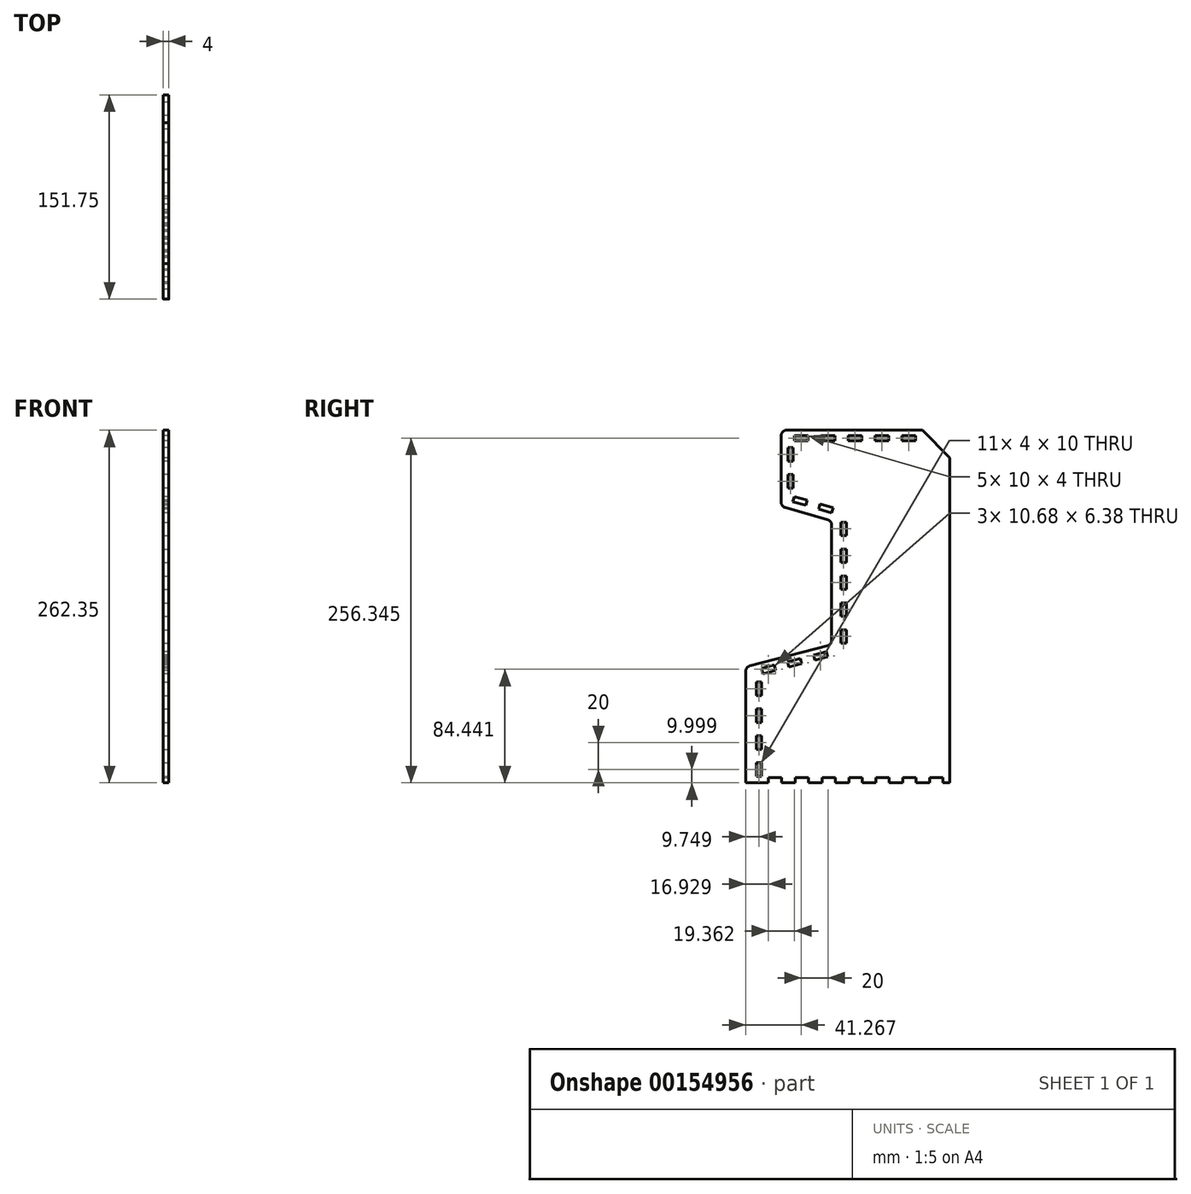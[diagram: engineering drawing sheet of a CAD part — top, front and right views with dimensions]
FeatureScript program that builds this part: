
annotation { "Feature Type Name" : "Feature", "Feature Type Description" : "" }
export const myFeature = defineFeature(function(context is Context, id is Id, definition is map)
    precondition{}
    {
        {
            var Q0;
            Q0=qCreatedBy(makeId("Right.planeOp"),FACE);
            var sketch = newSketch(context, id + "F0", { "sketchPlane" : qUnion([Q0])});
            skLineSegment(sketch, "E0", {"start": v(0, 0) * mm, "end": v(-63.83, -16.52) * mm});
            skLineSegment(sketch, "E1", {"start": v(-63.83, -16.52) * mm, "end": v(-63.83, -102.78) * mm});
            skLineSegment(sketch, "E2", {"start": v(-63.83, -102.78) * mm, "end": v(87.92, -102.78) * mm});
            skLineSegment(sketch, "E3", {"start": v(0, 0) * mm, "end": v(1, -3.87) * mm});
            skLineSegment(sketch, "E4", {"start": v(1, -3.87) * mm, "end": v(-3.84, -5.13) * mm});
            skLineSegment(sketch, "E5", {"start": v(-3.84, -5.13) * mm, "end": v(-13.52, -7.63) * mm});
            skLineSegment(sketch, "E6", {"start": v(-13.52, -7.63) * mm, "end": v(-23.2, -10.14) * mm});
            skLineSegment(sketch, "E7", {"start": v(-23.2, -10.14) * mm, "end": v(-32.88, -12.64) * mm});
            skLineSegment(sketch, "E8", {"start": v(-32.88, -12.64) * mm, "end": v(-42.56, -15.15) * mm});
            skLineSegment(sketch, "E9", {"start": v(-42.56, -15.15) * mm, "end": v(-52.24, -17.66) * mm});
            skLineSegment(sketch, "E10", {"start": v(-52.24, -17.66) * mm, "end": v(-61.92, -20.16) * mm});
            skLineSegment(sketch, "E11", {"start": v(-13.52, -7.63) * mm, "end": v(-12.52, -11.5) * mm});
            skLineSegment(sketch, "E12", {"start": v(-12.52, -11.5) * mm, "end": v(-2.84, -9) * mm});
            skLineSegment(sketch, "E13", {"start": v(-2.84, -9) * mm, "end": v(-3.84, -5.13) * mm});
            skLineSegment(sketch, "E14", {"start": v(-32.88, -12.64) * mm, "end": v(-31.88, -16.52) * mm});
            skLineSegment(sketch, "E15", {"start": v(-31.88, -16.52) * mm, "end": v(-22.2, -14) * mm});
            skLineSegment(sketch, "E16", {"start": v(-22.2, -14) * mm, "end": v(-23.2, -10.14) * mm});
            skLineSegment(sketch, "E17", {"start": v(-52.24, -17.66) * mm, "end": v(-51.24, -21.53) * mm});
            skLineSegment(sketch, "E18", {"start": v(-51.24, -21.53) * mm, "end": v(-41.56, -19.02) * mm});
            skLineSegment(sketch, "E19", {"start": v(-41.56, -19.02) * mm, "end": v(-42.56, -15.15) * mm});
            skLineSegment(sketch, "E20", {"start": v(0, 0) * mm, "end": v(0, 92.13) * mm});
            skLineSegment(sketch, "E21", {"start": v(87.92, -102.78) * mm, "end": v(87.92, 92.13) * mm});
            skLineSegment(sketch, "E22", {"start": v(0, 92.13) * mm, "end": v(87.92, 92.13) * mm});
            skSolve(sketch);
        }
        {
            var Q0;
            Q0 = qSketchRegion(id + "F0", true);
            extrude(context, id + "F1", {"entities" : qUnion([Q0]), "depth" : 4 * mm});
        }
        {
            var Q0;
            Q0=makeQuery(id+"F1.opExtrude","SWEPT_EDGE",EDGE,{"disambiguationData":[OSD([sQuery(id+"F0.wireOp",EDGE,"E0"),sQuery(id+"F0.wireOp",EDGE,"E1")])]});
            fillet(context, id + "F2", {"entities" : qUnion([Q0]), "radius" : 4 * mm, "tangentPropagation" : true, "allowEdgeOverflow" : false});
        }
        {
            var Q0;
            Q0=makeQuery(id+"F1.opExtrude","CAP_FACE",FACE,{"disambiguationData":[OSD([sQuery(id+"F0.wireOp",EDGE,"E0"),sQuery(id+"F0.wireOp",EDGE,"E1"),sQuery(id+"F0.wireOp",EDGE,"E2"),sQuery(id+"F0.wireOp",EDGE,"E5"),sQuery(id+"F0.wireOp",EDGE,"E7"),sQuery(id+"F0.wireOp",EDGE,"E9"),sQuery(id+"F0.wireOp",EDGE,"E11"),sQuery(id+"F0.wireOp",EDGE,"E12"),sQuery(id+"F0.wireOp",EDGE,"E13"),sQuery(id+"F0.wireOp",EDGE,"E14"),sQuery(id+"F0.wireOp",EDGE,"E15"),sQuery(id+"F0.wireOp",EDGE,"E16"),sQuery(id+"F0.wireOp",EDGE,"E17"),sQuery(id+"F0.wireOp",EDGE,"E18"),sQuery(id+"F0.wireOp",EDGE,"E19"),sQuery(id+"F0.wireOp",EDGE,"E20"),sQuery(id+"F0.wireOp",EDGE,"E21"),sQuery(id+"F0.wireOp",EDGE,"E22")])],"isStart":false});
            var sketch = newSketch(context, id + "F3", { "sketchPlane" : qUnion([Q0])});
            skLineSegment(sketch, "E23", {"start": v(-3.84, -5.13) * mm, "end": v(1, -3.87) * mm});
            skLineSegment(sketch, "E24", {"start": v(1, -3.87) * mm, "end": v(7, -3.87) * mm});
            skLineSegment(sketch, "E25", {"start": v(7, -3.87) * mm, "end": v(7, 92.13) * mm});
            skLineSegment(sketch, "E26", {"start": v(7, -3.87) * mm, "end": v(7, 1.13) * mm});
            skLineSegment(sketch, "E27", {"start": v(7, 1.13) * mm, "end": v(11, 1.13) * mm});
            skLineSegment(sketch, "E28", {"start": v(11, 1.13) * mm, "end": v(11, 11.13) * mm});
            skLineSegment(sketch, "E29", {"start": v(11, 11.13) * mm, "end": v(7, 11.13) * mm});
            skLineSegment(sketch, "E30.0.1.0", {"start": v(11, 31.13) * mm, "end": v(7, 31.13) * mm});
            skLineSegment(sketch, "E30.0.1.1", {"start": v(11, 21.13) * mm, "end": v(11, 31.13) * mm});
            skLineSegment(sketch, "E30.0.1.2", {"start": v(7, 21.13) * mm, "end": v(11, 21.13) * mm});
            skLineSegment(sketch, "E30.0.2.0", {"start": v(11, 51.13) * mm, "end": v(7, 51.13) * mm});
            skLineSegment(sketch, "E30.0.2.1", {"start": v(11, 41.13) * mm, "end": v(11, 51.13) * mm});
            skLineSegment(sketch, "E30.0.2.2", {"start": v(7, 41.13) * mm, "end": v(11, 41.13) * mm});
            skLineSegment(sketch, "E30.0.3.0", {"start": v(11, 71.13) * mm, "end": v(7, 71.13) * mm});
            skLineSegment(sketch, "E30.0.3.1", {"start": v(11, 61.13) * mm, "end": v(11, 71.13) * mm});
            skLineSegment(sketch, "E30.0.3.2", {"start": v(7, 61.13) * mm, "end": v(11, 61.13) * mm});
            skLineSegment(sketch, "E30.direction1", {"start": v(7, 11.13) * mm, "end": v(30, 11.13) * mm, "construction": true});
            skLineSegment(sketch, "E30.direction2", {"start": v(7, 11.13) * mm, "end": v(7, 31.13) * mm, "construction": true});
            skLineSegment(sketch, "E31.0.0.4", {"start": v(11, 91.13) * mm, "end": v(7, 91.13) * mm});
            skLineSegment(sketch, "E31.3.0.4", {"start": v(11, 81.13) * mm, "end": v(11, 91.13) * mm});
            skLineSegment(sketch, "E31.6.0.4", {"start": v(7, 81.13) * mm, "end": v(11, 81.13) * mm});
            skLineSegment(sketch, "E32", {"start": v(7, 91.13) * mm, "end": v(7, 81.13) * mm});
            skSolve(sketch);
        }
        {
            var Q0;
            Q0 = qSketchRegion(id + "F3", true);
            extrude(context, id + "F4", {"entities" : qUnion([Q0]), "operationType" : NewBodyOperationType.REMOVE, "oppositeDirection" : true, "depth" : 4 * mm});
        }
        {
            var Q0;
            Q0=makeQuery(id+"F1.opExtrude","CAP_FACE",FACE,{"disambiguationData":[OSD([sQuery(id+"F0.wireOp",EDGE,"E0"),sQuery(id+"F0.wireOp",EDGE,"E1"),sQuery(id+"F0.wireOp",EDGE,"E2"),sQuery(id+"F0.wireOp",EDGE,"E5"),sQuery(id+"F0.wireOp",EDGE,"E7"),sQuery(id+"F0.wireOp",EDGE,"E9"),sQuery(id+"F0.wireOp",EDGE,"E11"),sQuery(id+"F0.wireOp",EDGE,"E12"),sQuery(id+"F0.wireOp",EDGE,"E13"),sQuery(id+"F0.wireOp",EDGE,"E14"),sQuery(id+"F0.wireOp",EDGE,"E15"),sQuery(id+"F0.wireOp",EDGE,"E16"),sQuery(id+"F0.wireOp",EDGE,"E17"),sQuery(id+"F0.wireOp",EDGE,"E18"),sQuery(id+"F0.wireOp",EDGE,"E19"),sQuery(id+"F0.wireOp",EDGE,"E20"),sQuery(id+"F0.wireOp",EDGE,"E21"),sQuery(id+"F0.wireOp",EDGE,"E22")])],"isStart":false});
            var sketch = newSketch(context, id + "F5", { "sketchPlane" : qUnion([Q0])});
            skLineSegment(sketch, "E33", {"start": v(-51.24, -21.53) * mm, "end": v(-56.08, -22.78) * mm});
            skLineSegment(sketch, "E34", {"start": v(-56.08, -22.78) * mm, "end": v(-56.08, -27.78) * mm});
            skLineSegment(sketch, "E35", {"start": v(-56.08, -27.78) * mm, "end": v(-52.08, -27.78) * mm});
            skLineSegment(sketch, "E36", {"start": v(-56.08, -27.78) * mm, "end": v(-56.08, -37.78) * mm});
            skLineSegment(sketch, "E37", {"start": v(-56.08, -37.78) * mm, "end": v(-52.08, -37.78) * mm});
            skLineSegment(sketch, "E38", {"start": v(-52.08, -27.78) * mm, "end": v(-52.08, -37.78) * mm});
            skLineSegment(sketch, "E39.0.1.0", {"start": v(-52.08, -47.78) * mm, "end": v(-52.08, -57.78) * mm});
            skLineSegment(sketch, "E39.0.1.1", {"start": v(-56.08, -47.78) * mm, "end": v(-52.08, -47.78) * mm});
            skLineSegment(sketch, "E39.0.1.2", {"start": v(-56.08, -47.78) * mm, "end": v(-56.08, -57.78) * mm});
            skLineSegment(sketch, "E39.0.1.3", {"start": v(-56.08, -57.78) * mm, "end": v(-52.08, -57.78) * mm});
            skLineSegment(sketch, "E39.0.2.0", {"start": v(-52.08, -67.78) * mm, "end": v(-52.08, -77.78) * mm});
            skLineSegment(sketch, "E39.0.2.1", {"start": v(-56.08, -67.78) * mm, "end": v(-52.08, -67.78) * mm});
            skLineSegment(sketch, "E39.0.2.2", {"start": v(-56.08, -67.78) * mm, "end": v(-56.08, -77.78) * mm});
            skLineSegment(sketch, "E39.0.2.3", {"start": v(-56.08, -77.78) * mm, "end": v(-52.08, -77.78) * mm});
            skLineSegment(sketch, "E39.0.3.0", {"start": v(-52.08, -87.78) * mm, "end": v(-52.08, -97.78) * mm});
            skLineSegment(sketch, "E39.0.3.1", {"start": v(-56.08, -87.78) * mm, "end": v(-52.08, -87.78) * mm});
            skLineSegment(sketch, "E39.0.3.2", {"start": v(-56.08, -87.78) * mm, "end": v(-56.08, -97.78) * mm});
            skLineSegment(sketch, "E39.0.3.3", {"start": v(-56.08, -97.78) * mm, "end": v(-52.08, -97.78) * mm});
            skLineSegment(sketch, "E39.direction1", {"start": v(-52.08, -37.78) * mm, "end": v(-27.08, -37.78) * mm, "construction": true});
            skLineSegment(sketch, "E39.direction2", {"start": v(-52.08, -37.78) * mm, "end": v(-52.08, -57.78) * mm, "construction": true});
            skLineSegment(sketch, "E40", {"start": v(-52.08, -97.78) * mm, "end": v(-52.08, -102.78) * mm});
            skLineSegment(sketch, "E41", {"start": v(-52.08, -102.78) * mm, "end": v(-47.08, -102.78) * mm});
            skLineSegment(sketch, "E42.bottom", {"start": v(-47.08, -102.78) * mm, "end": v(-37.08, -102.78) * mm});
            skLineSegment(sketch, "E42.top", {"start": v(-47.08, -98.78) * mm, "end": v(-37.08, -98.78) * mm});
            skLineSegment(sketch, "E42.left", {"start": v(-47.08, -102.78) * mm, "end": v(-47.08, -98.78) * mm});
            skLineSegment(sketch, "E42.right", {"start": v(-37.08, -102.78) * mm, "end": v(-37.08, -98.78) * mm});
            skLineSegment(sketch, "E43.1.0.0", {"start": v(-27.08, -102.78) * mm, "end": v(-17.08, -102.78) * mm});
            skLineSegment(sketch, "E43.1.0.1", {"start": v(-17.08, -102.78) * mm, "end": v(-17.08, -98.78) * mm});
            skLineSegment(sketch, "E43.1.0.2", {"start": v(-27.08, -98.78) * mm, "end": v(-17.08, -98.78) * mm});
            skLineSegment(sketch, "E43.1.0.3", {"start": v(-27.08, -102.78) * mm, "end": v(-27.08, -98.78) * mm});
            skLineSegment(sketch, "E43.2.0.0", {"start": v(-7.08, -102.78) * mm, "end": v(2.92, -102.78) * mm});
            skLineSegment(sketch, "E43.2.0.1", {"start": v(2.92, -102.78) * mm, "end": v(2.92, -98.78) * mm});
            skLineSegment(sketch, "E43.2.0.2", {"start": v(-7.08, -98.78) * mm, "end": v(2.92, -98.78) * mm});
            skLineSegment(sketch, "E43.2.0.3", {"start": v(-7.08, -102.78) * mm, "end": v(-7.08, -98.78) * mm});
            skLineSegment(sketch, "E43.3.0.0", {"start": v(12.92, -102.78) * mm, "end": v(22.92, -102.78) * mm});
            skLineSegment(sketch, "E43.3.0.1", {"start": v(22.92, -102.78) * mm, "end": v(22.92, -98.78) * mm});
            skLineSegment(sketch, "E43.3.0.2", {"start": v(12.92, -98.78) * mm, "end": v(22.92, -98.78) * mm});
            skLineSegment(sketch, "E43.3.0.3", {"start": v(12.92, -102.78) * mm, "end": v(12.92, -98.78) * mm});
            skLineSegment(sketch, "E43.4.0.0", {"start": v(32.92, -102.78) * mm, "end": v(42.92, -102.78) * mm});
            skLineSegment(sketch, "E43.4.0.1", {"start": v(42.92, -102.78) * mm, "end": v(42.92, -98.78) * mm});
            skLineSegment(sketch, "E43.4.0.2", {"start": v(32.92, -98.78) * mm, "end": v(42.92, -98.78) * mm});
            skLineSegment(sketch, "E43.4.0.3", {"start": v(32.92, -102.78) * mm, "end": v(32.92, -98.78) * mm});
            skLineSegment(sketch, "E43.direction1", {"start": v(-47.08, -102.78) * mm, "end": v(-27.08, -102.78) * mm, "construction": true});
            skLineSegment(sketch, "E44.0.5.0", {"start": v(52.92, -102.78) * mm, "end": v(62.92, -102.78) * mm});
            skLineSegment(sketch, "E44.3.5.0", {"start": v(62.92, -102.78) * mm, "end": v(62.92, -98.78) * mm});
            skLineSegment(sketch, "E44.6.5.0", {"start": v(52.92, -98.78) * mm, "end": v(62.92, -98.78) * mm});
            skLineSegment(sketch, "E44.9.5.0", {"start": v(52.92, -102.78) * mm, "end": v(52.92, -98.78) * mm});
            skLineSegment(sketch, "E44.0.6.0", {"start": v(72.92, -102.78) * mm, "end": v(82.92, -102.78) * mm});
            skLineSegment(sketch, "E44.3.6.0", {"start": v(82.92, -102.78) * mm, "end": v(82.92, -98.78) * mm});
            skLineSegment(sketch, "E44.6.6.0", {"start": v(72.92, -98.78) * mm, "end": v(82.92, -98.78) * mm});
            skLineSegment(sketch, "E44.9.6.0", {"start": v(72.92, -102.78) * mm, "end": v(72.92, -98.78) * mm});
            skSolve(sketch);
        }
        {
            var Q0;
            Q0=makeQuery(id+"F5.imprint","IMPRINT",FACE,{"disambiguationData":[TD([[makeQuery(id+"F5.imprint","IMPRINT",EDGE,{"derivedFrom":sQuery(id+"F5.wireOp",EDGE,"E35")}),-1.0]])]});
            var Q1;
            Q1=makeQuery(id+"F5.imprint","IMPRINT",FACE,{"disambiguationData":[TD([[makeQuery(id+"F5.imprint","IMPRINT",EDGE,{"derivedFrom":sQuery(id+"F5.wireOp",EDGE,"E39.0.1.0")}),-1.0]])]});
            var Q2;
            Q2=makeQuery(id+"F5.imprint","IMPRINT",FACE,{"disambiguationData":[TD([[makeQuery(id+"F5.imprint","IMPRINT",EDGE,{"derivedFrom":sQuery(id+"F5.wireOp",EDGE,"E39.0.2.0")}),-1.0]])]});
            var Q3;
            Q3=makeQuery(id+"F5.imprint","IMPRINT",FACE,{"disambiguationData":[TD([[makeQuery(id+"F5.imprint","IMPRINT",EDGE,{"derivedFrom":sQuery(id+"F5.wireOp",EDGE,"E39.0.3.0")}),-1.0]])]});
            var Q4;
            Q4=makeQuery(id+"F5.imprint","IMPRINT",FACE,{"disambiguationData":[TD([[makeQuery(id+"F5.imprint","IMPRINT",EDGE,{"derivedFrom":sQuery(id+"F5.wireOp",EDGE,"E43.2.0.0")}),1.0]])]});
            var Q5;
            Q5=makeQuery(id+"F5.imprint","IMPRINT",FACE,{"disambiguationData":[TD([[makeQuery(id+"F5.imprint","IMPRINT",EDGE,{"derivedFrom":sQuery(id+"F5.wireOp",EDGE,"E43.3.0.0")}),1.0]])]});
            var Q6;
            Q6=makeQuery(id+"F5.imprint","IMPRINT",FACE,{"disambiguationData":[TD([[makeQuery(id+"F5.imprint","IMPRINT",EDGE,{"derivedFrom":sQuery(id+"F5.wireOp",EDGE,"E43.4.0.0")}),1.0]])]});
            var Q7;
            Q7=makeQuery(id+"F5.imprint","IMPRINT",FACE,{"disambiguationData":[TD([[makeQuery(id+"F5.imprint","IMPRINT",EDGE,{"derivedFrom":sQuery(id+"F5.wireOp",EDGE,"E43.1.0.0")}),1.0]])]});
            var Q8;
            Q8=makeQuery(id+"F5.imprint","IMPRINT",FACE,{"disambiguationData":[TD([[makeQuery(id+"F5.imprint","IMPRINT",EDGE,{"derivedFrom":sQuery(id+"F5.wireOp",EDGE,"E42.bottom")}),1.0]])]});
            var Q9;
            Q9=makeQuery(id+"F5.imprint","IMPRINT",FACE,{"disambiguationData":[TD([[makeQuery(id+"F5.imprint","IMPRINT",EDGE,{"derivedFrom":sQuery(id+"F5.wireOp",EDGE,"E44.0.5.0")}),1.0]])]});
            var Q10;
            Q10=makeQuery(id+"F5.imprint","IMPRINT",FACE,{"disambiguationData":[TD([[makeQuery(id+"F5.imprint","IMPRINT",EDGE,{"derivedFrom":sQuery(id+"F5.wireOp",EDGE,"E44.0.6.0")}),1.0]])]});
            extrude(context, id + "F6", {"entities" : qUnion([Q0, Q1, Q2, Q3, Q4, Q5, Q6, Q7, Q8, Q9, Q10]), "operationType" : NewBodyOperationType.REMOVE, "oppositeDirection" : true, "depth" : 4 * mm});
        }
        {
            var Q0;
            Q0=makeQuery(id+"F1.opExtrude","CAP_FACE",FACE,{"disambiguationData":[OSD([sQuery(id+"F0.wireOp",EDGE,"E0"),sQuery(id+"F0.wireOp",EDGE,"E1"),sQuery(id+"F0.wireOp",EDGE,"E2"),sQuery(id+"F0.wireOp",EDGE,"E5"),sQuery(id+"F0.wireOp",EDGE,"E7"),sQuery(id+"F0.wireOp",EDGE,"E9"),sQuery(id+"F0.wireOp",EDGE,"E11"),sQuery(id+"F0.wireOp",EDGE,"E12"),sQuery(id+"F0.wireOp",EDGE,"E13"),sQuery(id+"F0.wireOp",EDGE,"E14"),sQuery(id+"F0.wireOp",EDGE,"E15"),sQuery(id+"F0.wireOp",EDGE,"E16"),sQuery(id+"F0.wireOp",EDGE,"E17"),sQuery(id+"F0.wireOp",EDGE,"E18"),sQuery(id+"F0.wireOp",EDGE,"E19"),sQuery(id+"F0.wireOp",EDGE,"E20"),sQuery(id+"F0.wireOp",EDGE,"E21"),sQuery(id+"F0.wireOp",EDGE,"E22")])],"isStart":false});
            var sketch = newSketch(context, id + "F7", { "sketchPlane" : qUnion([Q0])});
            skLineSegment(sketch, "E45", {"start": v(0, 92.13) * mm, "end": v(-37.5, 102.82) * mm});
            skLineSegment(sketch, "E46", {"start": v(-37.5, 102.82) * mm, "end": v(-37.5, 159.57) * mm});
            skLineSegment(sketch, "E47", {"start": v(-37.5, 159.57) * mm, "end": v(87.92, 159.57) * mm});
            skLineSegment(sketch, "E48", {"start": v(87.92, 159.57) * mm, "end": v(87.92, 92.13) * mm});
            skSolve(sketch);
        }
        {
            var Q0;
            Q0=makeQuery(id+"F7.imprint","IMPRINT",FACE,{"disambiguationData":[TD([[makeQuery(id+"F7.imprint","IMPRINT",EDGE,{"derivedFrom":sQuery(id+"F7.wireOp",EDGE,"E45")}),-1.0]])]});
            extrude(context, id + "F8", {"entities" : qUnion([Q0]), "operationType" : NewBodyOperationType.ADD, "oppositeDirection" : true, "depth" : 4 * mm});
        }
        {
            var Q0;
            Q0=makeQuery(id+"F8.opExtrude","SWEPT_EDGE",EDGE,{"disambiguationData":[OSD([sQuery(id+"F7.wireOp",EDGE,"E46"),sQuery(id+"F7.wireOp",EDGE,"E47")])]});
            var Q1;
            Q1=makeQuery(id+"F8.opExtrude","SWEPT_EDGE",EDGE,{"disambiguationData":[OSD([sQuery(id+"F7.wireOp",EDGE,"E47"),sQuery(id+"F7.wireOp",EDGE,"E48")])]});
            var Q2;
            Q2=makeQuery(id+"F8.opExtrude","SWEPT_EDGE",EDGE,{"disambiguationData":[OSD([sQuery(id+"F7.wireOp",EDGE,"E45"),sQuery(id+"F7.wireOp",EDGE,"E46")])]});
            fillet(context, id + "F9", {"entities" : qUnion([Q0, Q1, Q2]), "radius" : 4 * mm, "tangentPropagation" : true, "allowEdgeOverflow" : false});
        }
        {
            var Q0;
            {var subQ0=sQuery(id+"F0.wireOp",EDGE,"E22");Q0=makeQuery(id+"F8.boolean.opBoolean","MERGE",FACE,{"derivedFrom":[makeQuery(id+"F1.opExtrude","CAP_FACE",FACE,{"disambiguationData":[OSD([sQuery(id+"F0.wireOp",EDGE,"E0"),sQuery(id+"F0.wireOp",EDGE,"E1"),sQuery(id+"F0.wireOp",EDGE,"E2"),sQuery(id+"F0.wireOp",EDGE,"E5"),sQuery(id+"F0.wireOp",EDGE,"E7"),sQuery(id+"F0.wireOp",EDGE,"E9"),sQuery(id+"F0.wireOp",EDGE,"E11"),sQuery(id+"F0.wireOp",EDGE,"E12"),sQuery(id+"F0.wireOp",EDGE,"E13"),sQuery(id+"F0.wireOp",EDGE,"E14"),sQuery(id+"F0.wireOp",EDGE,"E15"),sQuery(id+"F0.wireOp",EDGE,"E16"),sQuery(id+"F0.wireOp",EDGE,"E17"),sQuery(id+"F0.wireOp",EDGE,"E18"),sQuery(id+"F0.wireOp",EDGE,"E19"),sQuery(id+"F0.wireOp",EDGE,"E20"),sQuery(id+"F0.wireOp",EDGE,"E21"),subQ0])],"isStart":true}),makeQuery(id+"F8.opExtrude","CAP_FACE",FACE,{"disambiguationData":[OSD([subQ0,sQuery(id+"F7.wireOp",EDGE,"E45"),sQuery(id+"F7.wireOp",EDGE,"E46"),sQuery(id+"F7.wireOp",EDGE,"E47"),sQuery(id+"F7.wireOp",EDGE,"E48")])],"isStart":false})]});}
            var sketch = newSketch(context, id + "F10", { "sketchPlane" : qUnion([Q0])});
            skLineSegment(sketch, "E49", {"start": v(-7, 91.13) * mm, "end": v(-7, 96.13) * mm});
            skLineSegment(sketch, "E50", {"start": v(-7, 96.13) * mm, "end": v(0, 98.12) * mm});
            skLineSegment(sketch, "E51", {"start": v(0, 98.12) * mm, "end": v(9.62, 100.87) * mm});
            skLineSegment(sketch, "E52", {"start": v(9.62, 100.87) * mm, "end": v(19.23, 103.6) * mm});
            skLineSegment(sketch, "E53", {"start": v(19.23, 103.6) * mm, "end": v(28.85, 106.35) * mm});
            skLineSegment(sketch, "E54", {"start": v(28.85, 106.35) * mm, "end": v(37.5, 108.81) * mm});
            skLineSegment(sketch, "E55", {"start": v(0, 98.12) * mm, "end": v(-1.1, 101.97) * mm});
            skLineSegment(sketch, "E56", {"start": v(-1.1, 101.97) * mm, "end": v(8.52, 104.71) * mm});
            skLineSegment(sketch, "E57", {"start": v(8.52, 104.71) * mm, "end": v(9.62, 100.87) * mm});
            skLineSegment(sketch, "E58", {"start": v(19.23, 103.6) * mm, "end": v(18.14, 107.45) * mm});
            skLineSegment(sketch, "E59", {"start": v(18.14, 107.45) * mm, "end": v(27.75, 110.2) * mm});
            skLineSegment(sketch, "E60", {"start": v(27.75, 110.2) * mm, "end": v(28.85, 106.35) * mm});
            skLineSegment(sketch, "E61", {"start": v(27.75, 110.2) * mm, "end": v(32.56, 111.57) * mm});
            skLineSegment(sketch, "E62", {"start": v(32.56, 111.57) * mm, "end": v(32.56, 116.57) * mm});
            skLineSegment(sketch, "E63", {"start": v(32.56, 116.57) * mm, "end": v(32.56, 126.57) * mm});
            skLineSegment(sketch, "E64", {"start": v(32.56, 126.57) * mm, "end": v(32.56, 131.57) * mm});
            skPoint(sketch, "E64.endSnap0", {"position": v(32.56, 121.57) * mm});
            skLineSegment(sketch, "E65", {"start": v(32.56, 131.57) * mm, "end": v(32.56, 159.57) * mm});
            skLineSegment(sketch, "E66", {"start": v(32.56, 126.57) * mm, "end": v(28.56, 126.57) * mm});
            skLineSegment(sketch, "E67", {"start": v(28.56, 126.57) * mm, "end": v(28.56, 126.57) * mm});
            skLineSegment(sketch, "E68", {"start": v(28.56, 126.57) * mm, "end": v(28.56, 116.57) * mm});
            skLineSegment(sketch, "E69", {"start": v(28.56, 116.57) * mm, "end": v(32.56, 116.57) * mm});
            skLineSegment(sketch, "E70.0.1.0", {"start": v(28.56, 146.57) * mm, "end": v(28.56, 136.57) * mm});
            skLineSegment(sketch, "E70.0.1.1", {"start": v(32.56, 146.57) * mm, "end": v(28.56, 146.57) * mm});
            skLineSegment(sketch, "E70.0.1.2", {"start": v(32.56, 136.57) * mm, "end": v(32.56, 146.57) * mm});
            skLineSegment(sketch, "E70.0.1.3", {"start": v(28.56, 136.57) * mm, "end": v(32.56, 136.57) * mm});
            skLineSegment(sketch, "E70.direction2", {"start": v(28.56, 116.57) * mm, "end": v(28.56, 136.57) * mm, "construction": true});
            skLineSegment(sketch, "E71", {"start": v(28.56, 146.57) * mm, "end": v(28.56, 151.57) * mm});
            skLineSegment(sketch, "E72", {"start": v(28.56, 151.57) * mm, "end": v(27.56, 151.57) * mm});
            skLineSegment(sketch, "E73", {"start": v(27.56, 151.57) * mm, "end": v(27.56, 155.57) * mm});
            skLineSegment(sketch, "E74", {"start": v(27.56, 155.57) * mm, "end": v(17.56, 155.57) * mm});
            skLineSegment(sketch, "E75", {"start": v(27.56, 151.57) * mm, "end": v(17.56, 151.57) * mm});
            skLineSegment(sketch, "E76", {"start": v(17.56, 151.57) * mm, "end": v(17.56, 155.57) * mm});
            skLineSegment(sketch, "E77.1.0.0", {"start": v(-2.44, 151.57) * mm, "end": v(-2.44, 155.57) * mm});
            skLineSegment(sketch, "E77.1.0.1", {"start": v(7.56, 151.57) * mm, "end": v(-2.44, 151.57) * mm});
            skLineSegment(sketch, "E77.1.0.2", {"start": v(7.56, 151.57) * mm, "end": v(7.56, 155.57) * mm});
            skLineSegment(sketch, "E77.1.0.3", {"start": v(7.56, 155.57) * mm, "end": v(-2.44, 155.57) * mm});
            skLineSegment(sketch, "E77.2.0.0", {"start": v(-22.44, 151.57) * mm, "end": v(-22.44, 155.57) * mm});
            skLineSegment(sketch, "E77.2.0.1", {"start": v(-12.44, 151.57) * mm, "end": v(-22.44, 151.57) * mm});
            skLineSegment(sketch, "E77.2.0.2", {"start": v(-12.44, 151.57) * mm, "end": v(-12.44, 155.57) * mm});
            skLineSegment(sketch, "E77.2.0.3", {"start": v(-12.44, 155.57) * mm, "end": v(-22.44, 155.57) * mm});
            skLineSegment(sketch, "E77.3.0.0", {"start": v(-42.44, 151.57) * mm, "end": v(-42.44, 155.57) * mm});
            skLineSegment(sketch, "E77.3.0.1", {"start": v(-32.44, 151.57) * mm, "end": v(-42.44, 151.57) * mm});
            skLineSegment(sketch, "E77.3.0.2", {"start": v(-32.44, 151.57) * mm, "end": v(-32.44, 155.57) * mm});
            skLineSegment(sketch, "E77.3.0.3", {"start": v(-32.44, 155.57) * mm, "end": v(-42.44, 155.57) * mm});
            skLineSegment(sketch, "E77.4.0.0", {"start": v(-62.44, 151.57) * mm, "end": v(-62.44, 155.57) * mm});
            skLineSegment(sketch, "E77.4.0.1", {"start": v(-52.44, 151.57) * mm, "end": v(-62.44, 151.57) * mm});
            skLineSegment(sketch, "E77.4.0.2", {"start": v(-52.44, 151.57) * mm, "end": v(-52.44, 155.57) * mm});
            skLineSegment(sketch, "E77.4.0.3", {"start": v(-52.44, 155.57) * mm, "end": v(-62.44, 155.57) * mm});
            skLineSegment(sketch, "E77.direction1", {"start": v(17.56, 151.57) * mm, "end": v(-2.44, 151.57) * mm, "construction": true});
            skLineSegment(sketch, "E78", {"start": v(-62.44, 155.57) * mm, "end": v(-71.44, 155.57) * mm});
            skLineSegment(sketch, "E79", {"start": v(-71.44, 155.57) * mm, "end": v(-80.7, 146.3) * mm});
            skLineSegment(sketch, "E80", {"start": v(-71.44, 155.57) * mm, "end": v(-87.92, 139.08) * mm});
            skLineSegment(sketch, "E81", {"start": v(-87.92, 139.08) * mm, "end": v(-87.92, 159.57) * mm});
            skLineSegment(sketch, "E82", {"start": v(-80.7, 146.3) * mm, "end": v(-67.44, 159.57) * mm});
            skLineSegment(sketch, "E83", {"start": v(-67.44, 159.57) * mm, "end": v(-87.92, 159.57) * mm});
            skSolve(sketch);
        }
        {
            var Q0;
            Q0 = qSketchRegion(id + "F10", true);
            extrude(context, id + "F11", {"entities" : qUnion([Q0]), "operationType" : NewBodyOperationType.REMOVE, "oppositeDirection" : true, "depth" : 25 * mm});
        }
        {
            var Q0;
            Q0=makeQuery(id+"F11.boolean.opBoolean","COPY",EDGE,{"derivedFrom":makeQuery(id+"F11.opExtrude","SWEPT_EDGE",EDGE,{"disambiguationData":[OSD([sQuery(id+"F7.wireOp",EDGE,"E47"),sQuery(id+"F10.wireOp",EDGE,"E82"),sQuery(id+"F10.wireOp",EDGE,"E83")])]})});
            var Q1;
            Q1=makeQuery(id+"F11.boolean.opBoolean","COPY",EDGE,{"derivedFrom":makeQuery(id+"F11.opExtrude","SWEPT_EDGE",EDGE,{"disambiguationData":[OSD([sQuery(id+"F0.wireOp",EDGE,"E21"),sQuery(id+"F7.wireOp",EDGE,"E48"),sQuery(id+"F10.wireOp",EDGE,"E80"),sQuery(id+"F10.wireOp",EDGE,"E81")])]})});
            var Q2;
            {var subQ0=sQuery(id+"F0.wireOp",EDGE,"E22");var subQ1=sQuery(id+"F0.wireOp",EDGE,"E20");Q2=makeQuery(id+"F8.boolean.opBoolean","MERGE",EDGE,{"derivedFrom":[makeQuery(id+"F1.opExtrude","SWEPT_EDGE",EDGE,{"disambiguationData":[OSD([subQ1,subQ0])]}),makeQuery(id+"F8.opExtrude","SWEPT_EDGE",EDGE,{"disambiguationData":[OSD([subQ1,subQ0,sQuery(id+"F7.wireOp",EDGE,"E45")])]})]});}
            var Q3;
            Q3=makeQuery(id+"F1.opExtrude","SWEPT_EDGE",EDGE,{"disambiguationData":[OSD([sQuery(id+"F0.wireOp",EDGE,"E0"),sQuery(id+"F0.wireOp",EDGE,"E20")])]});
            fillet(context, id + "F12", {"entities" : qUnion([Q0, Q1, Q2, Q3]), "radius" : 4 * mm, "tangentPropagation" : true, "allowEdgeOverflow" : false});
        }
    });
